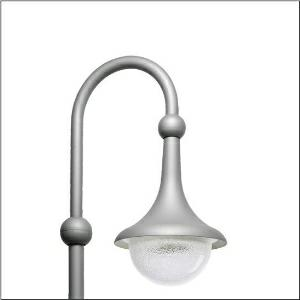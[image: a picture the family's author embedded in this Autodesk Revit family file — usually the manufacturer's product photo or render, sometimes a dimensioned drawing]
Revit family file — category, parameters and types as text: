
# Revit family: kleine_glocke___st1_2a_5xa1573k1b208_586f
name_source: partatom
category: Lighting Fixtures
units: mm (PartAtom-declared; Revit-internal decimal feet)

## family parameters
Cut with Voids When Loaded = No
Host = Face
Light Source = No
Part Type = Normal
Room Calculation Point = No
Round Connector Dimension = Use Diameter
Shared = No

## types (1)
- --- (1 x LED, 1750 lm, 13.2 W, 4000K)
    Apparent Load = 13 VA
    CIE Flux Codes = 28 64 93 98 100
    Color Rendering = 70
    Color Temperature = 4000K
    Default Elevation = 1800 mm
    Description = Small Bell, mast luminaire, primary light control with 3 zone facetted reflector, of plastic, aluminium vaporised, primary optical cover: enclosure, of PMMA, transparent structured, light distribution: ST1.2a, light emission: direct distribution, primary light characteristic: asymmetric, installation type: suspended mounting, LED High Power LED, rated luminous flux: 1.750 lm, light colour: 740, colour temperature: 4000K, control gear: ECG Plus, control: flexible luminous flux parameterisation, time-dependent luminous flux control, constant luminous flux control, digital communication interface, power reduction, electronic power reduction, mains connection: 220..240V, AC, 50/60Hz, start of lifetime: 13 W, end of lifetime: 14 W, reduction: 7 W, luminaire housing, bell-shaped, of glass-fibre reinforced polyester, coated, Siteco® metallic grey (DB 702S), diameter: 430 mm, height: 575mm, protection rating (complete): IP54, insulation class (complete): insulation class II (safety insulation), certification: CE, ENEC, VDE, impact resistance: IK07, standard-compliant lighting for roads and squares, packaging unit: 1 piece

Light Distribution: ST1.2a
    Height = 575 mm
    Lamp = 1 x LED
    Lamp Light Flux = 1750 lm
    Lamp Power = 13.2 W
    Lamp count = 1
    Length = 430 mm
    Luminous efficacy = 133 lm/W
    Manufacturer = Siteco
    ModVariant = No
    Model = 5XA1573K1B208
    Number of Poles = 1
    OnlyDefault = Yes
    Power Factor = 1
    Product Name = Kleine Glocke | ST1.2a
    Product group = mast luminaire | pylon annexe
    ProductGroupID = 6200
    Protection Class = Protection class II
    Protection Degree = IP 54
    RLX_Detail_Level = 1
    RlxData = <blob elided: 52049 chars, md5=b03c70ac>
    Socket = socket
    Standby Power = 0 W
    System Light Flux = 1750 lm
    System Power = 13 W
    Type Comments = factory setting: luminous flux: 100 % | dim-lin: 254 | 249 mA
    Type Image = l_1003770.jpg
    URL = http://relux.com
    VarID = @adj_130649
    Voltage = 0 V
    Weight = 0.00 kg
    Width = 0 mm  [stored 0 ft]

note: [stored X ft] marks values corroborated as IEEE doubles in the binary element streams (Revit-internal decimal feet)

## geometry (parser evidence)
native form markers: Blend x4, Sweep x13
no freeform markers — native parametric forms only
